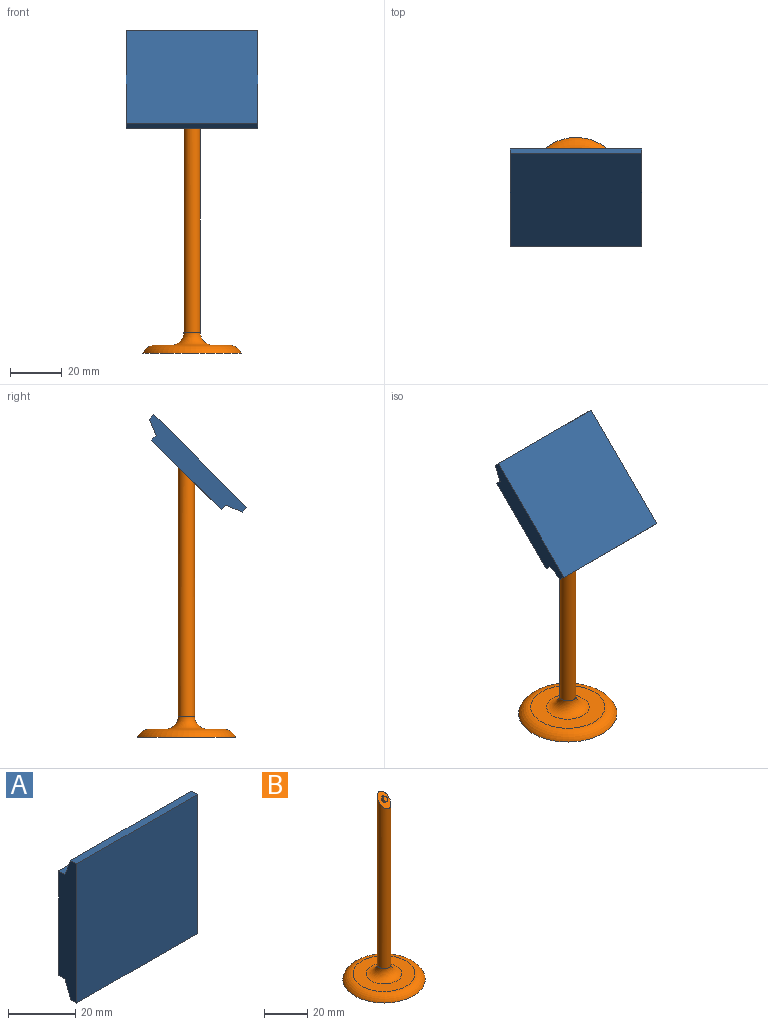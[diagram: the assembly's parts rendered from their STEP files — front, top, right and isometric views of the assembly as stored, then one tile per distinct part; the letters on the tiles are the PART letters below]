
ASSEMBLY  parts=2 mates=1
PART A: 15 faces, bbox 50.8x7.6x50.8 mm
  f0: plane 50.8x38.1mm, normal (0,1,0), area 1930mm2, adj f1,f7,f8,f9,f10,f11,f12,f13
  f1: plane 50.8x2.54mm, normal (0,0,1), area 129mm2, adj f0,f2,f8,f9
  f2: plane 50.8x6.35mm, normal (0,0.93,0.37), area 347.4mm2, adj f1,f3,f8,f9
  f3: plane 50.8x2.54mm, normal (0,0,1), area 129mm2, adj f2,f4,f8,f9
  f4: plane 50.8x50.8mm, normal (0,-1,0), area 2580.6mm2, adj f3,f5,f8,f9
  f5: plane 50.8x2.54mm, normal (0,0,-1), area 129mm2, adj f4,f6,f8,f9
  f6: plane 50.8x6.35mm, normal (0,0.93,-0.37), area 347.4mm2, adj f5,f7,f8,f9
  f7: plane 50.8x2.54mm, normal (0,0,-1), area 129mm2, adj f0,f6,f8,f9
  f8: plane 50.8x7.62mm, normal (1,0,0), area 338.7mm2, adj f0,f1,f2,f3,f4,f5,f6,f7
  f9: plane 50.8x7.62mm, normal (-1,0,0), area 338.7mm2, adj f0,f1,f2,f3,f4,f5,f6,f7
  f10: cylinder r=1.27mm len=2.54mm, axis (0,1,0), area 9.5mm2, adj f0,f11,f13,f14
  f11: plane 1.27x0.79mm, normal (1,0,0), area 1mm2, adj f0,f10,f12,f14
  f12: plane 1.27x0.51mm, normal (0,0,-1), area 0.6mm2, adj f0,f11,f13,f14
  f13: plane 1.27x0.79mm, normal (-1,0,0), area 1mm2, adj f0,f10,f12,f14
  f14: plane 3.3x2.54mm, normal (0,1,0), area 5.5mm2, adj f10,f11,f12,f13
PART B: 11 faces, bbox 43.4x43.4x108 mm
  f0: cylinder r=3.17mm len=96.52mm, axis (0,0,1), area 1860mm2, adj f1,f5
  f1: plane 7.69x7.69mm, normal (0,-0.71,0.71), area 39.3mm2, adj f0,f6,f7,f8,f9
  f2: plane 28.68x28.68mm, normal (0,0,1), area 432mm2, adj f4,f5
  f3: plane 38.1x38.1mm, normal (0,0,-1), area 1140.1mm2, adj f4
  f4: torus R=14.34mm, axis (0,0,-1), area 644.4mm2, adj f2,f3
  f5: torus R=8.26mm, axis (0,0,1), area 251.7mm2, adj f0,f2
  f6: cylinder r=1.27mm len=2.68mm, axis (0,0.71,-0.71), area 9.5mm2, adj f1,f7,f9,f10
  f7: plane 1.45x1.45mm, normal (1,0,0), area 1mm2, adj f1,f6,f8,f10
  f8: plane 0.9x0.9mm, normal (0,0.71,0.71), area 0.6mm2, adj f1,f7,f9,f10
  f9: plane 1.46x1.46mm, normal (-1,0,0), area 1mm2, adj f1,f6,f8,f10
  f10: plane 2.54x2.34mm, normal (0,-0.71,0.71), area 5.5mm2, adj f6,f7,f8,f9
PLACE A rot(axis=(-1,0,0),45deg) t=(-5.99,5.12,62.09)mm
PLACE B t=(-5.99,5.12,14.46)mm fixed
MATE pin_slot B.f6 <-> A.f10  axis (0,-0.71,0.71) through (-5.99,5.12,62.09)mm
